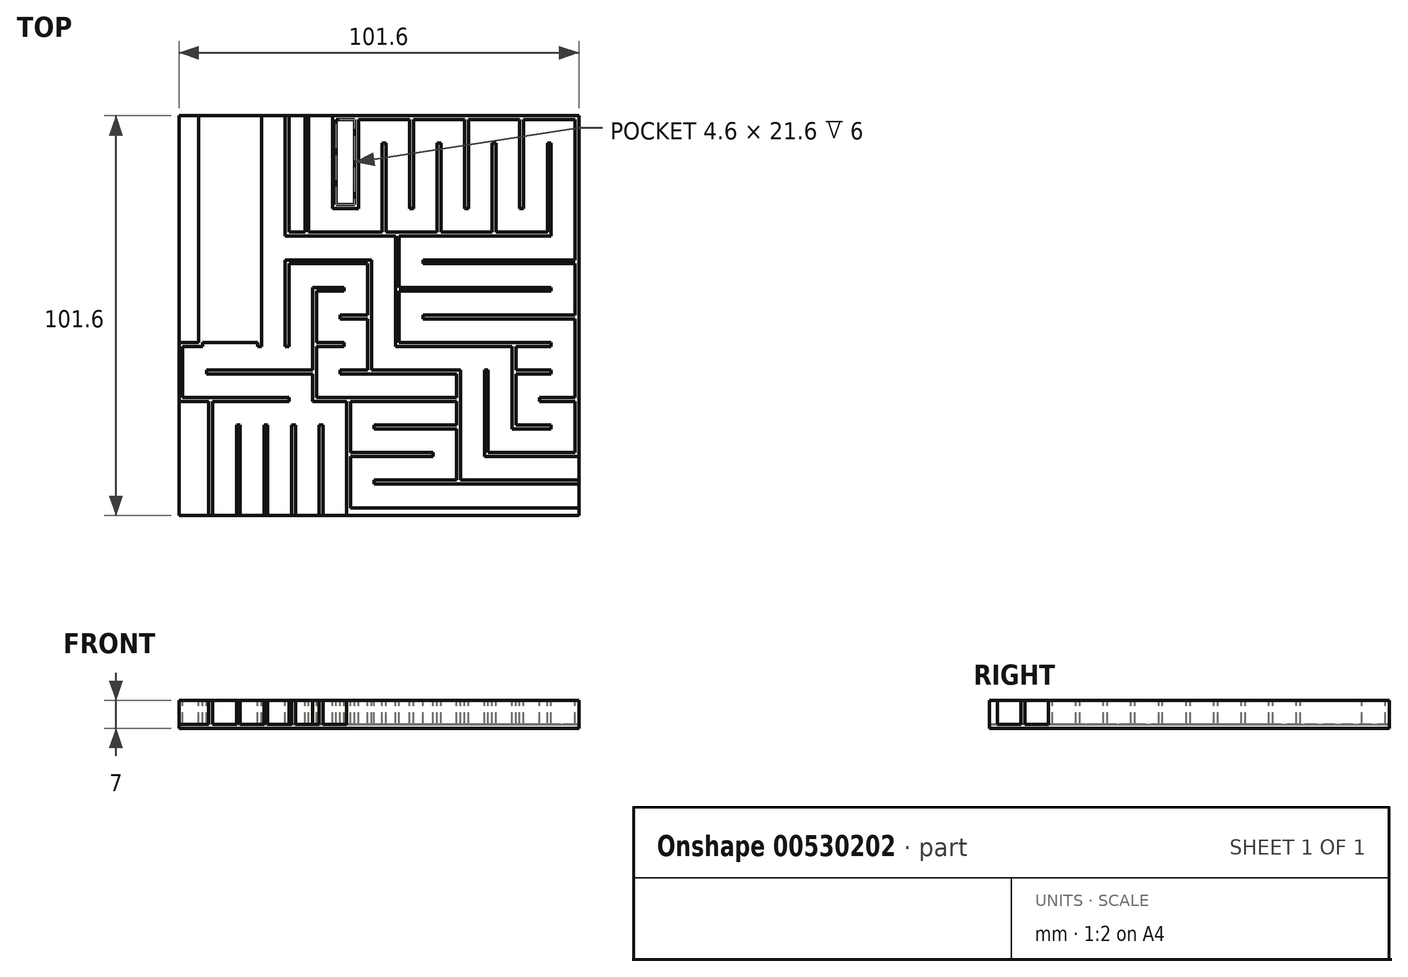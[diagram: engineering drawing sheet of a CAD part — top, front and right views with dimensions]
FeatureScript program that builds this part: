
annotation { "Feature Type Name" : "Feature", "Feature Type Description" : "" }
export const myFeature = defineFeature(function(context is Context, id is Id, definition is map)
    precondition{}
    {
        {
            var Q0;
            Q0=qCreatedBy(makeId("Top.planeOp"),FACE);
            var sketch = newSketch(context, id + "F0", { "sketchPlane" : qUnion([Q0])});
            skLineSegment(sketch, "E0.bottom", {"start": v(50.8, 50.8) * mm, "end": v(-50.8, 50.8) * mm});
            skLineSegment(sketch, "E0.top", {"start": v(50.8, -50.8) * mm, "end": v(-50.8, -50.8) * mm});
            skLineSegment(sketch, "E0.left", {"start": v(50.8, 50.8) * mm, "end": v(50.8, -50.8) * mm});
            skLineSegment(sketch, "E0.right", {"start": v(-50.8, 50.8) * mm, "end": v(-50.8, -50.8) * mm});
            skPoint(sketch, "E0.middle", {"position": v(0, 0) * mm});
            skSolve(sketch);
        }
        {
            var Q0;
            Q0=makeQuery(id+"F0.imprint","IMPRINT",FACE,{"disambiguationData":[TD([[makeQuery(id+"F0.imprint","IMPRINT",EDGE,{"derivedFrom":sQuery(id+"F0.wireOp",EDGE,"E0.bottom")}),1.0]])]});
            extrude(context, id + "F1", {"entities" : qUnion([Q0]), "depth" : 7 * mm, "offsetDistance" : 25.4 * mm});
        }
        {
            var Q0;
            Q0=makeQuery(id+"F1.opExtrude","CAP_FACE",FACE,{"disambiguationData":[OSD([sQuery(id+"F0.wireOp",EDGE,"E0.bottom"),sQuery(id+"F0.wireOp",EDGE,"E0.top"),sQuery(id+"F0.wireOp",EDGE,"E0.left"),sQuery(id+"F0.wireOp",EDGE,"E0.right")])],"isStart":false});
            var sketch = newSketch(context, id + "F2", { "sketchPlane" : qUnion([Q0])});
            skPoint(sketch, "E1", {"position": v(50.8, -48.8) * mm});
            skPoint(sketch, "E2", {"position": v(50.8, -42.8) * mm});
            skPoint(sketch, "E3", {"position": v(-1.2, -41.8) * mm});
            skLineSegment(sketch, "E4.bottom", {"start": v(-1.2, -41.8) * mm, "end": v(50.8, -41.8) * mm});
            skLineSegment(sketch, "E4.top", {"start": v(-1.2, -42.8) * mm, "end": v(50.8, -42.8) * mm});
            skLineSegment(sketch, "E4.left", {"start": v(-1.2, -41.8) * mm, "end": v(-1.2, -42.8) * mm});
            skLineSegment(sketch, "E4.right", {"start": v(50.8, -41.8) * mm, "end": v(50.8, -42.8) * mm});
            skPoint(sketch, "E5", {"position": v(13.8, -35.8) * mm});
            skPoint(sketch, "E6", {"position": v(-8.2, -34.8) * mm});
            skLineSegment(sketch, "E7.bottom", {"start": v(13.8, -35.8) * mm, "end": v(-8.2, -35.8) * mm});
            skLineSegment(sketch, "E7.top", {"start": v(13.8, -34.8) * mm, "end": v(-8.2, -34.8) * mm});
            skLineSegment(sketch, "E7.left", {"start": v(13.8, -35.8) * mm, "end": v(13.8, -34.8) * mm});
            skLineSegment(sketch, "E7.right", {"start": v(-8.2, -35.8) * mm, "end": v(-8.2, -34.8) * mm});
            skPoint(sketch, "E8", {"position": v(-7.2, -50.8) * mm});
            skLineSegment(sketch, "E9.bottom", {"start": v(-7.2, -50.8) * mm, "end": v(-8.2, -50.8) * mm});
            skLineSegment(sketch, "E9.top", {"start": v(-7.2, -34.8) * mm, "end": v(-8.2, -34.8) * mm});
            skLineSegment(sketch, "E9.left", {"start": v(-7.2, -50.8) * mm, "end": v(-7.2, -34.8) * mm});
            skLineSegment(sketch, "E9.right", {"start": v(-8.2, -50.8) * mm, "end": v(-8.2, -34.8) * mm});
            skLineSegment(sketch, "E10", {"start": v(50.8, -48.8) * mm, "end": v(-7.2, -48.8) * mm});
            skPoint(sketch, "E11", {"position": v(19.8, -28.8) * mm});
            skLineSegment(sketch, "E12", {"start": v(19.8, -28.8) * mm, "end": v(19.8, -41.8) * mm});
            skPoint(sketch, "E13", {"position": v(-1.2, -27.8) * mm});
            skLineSegment(sketch, "E14.bottom", {"start": v(-1.2, -27.8) * mm, "end": v(19.8, -27.8) * mm});
            skLineSegment(sketch, "E14.top", {"start": v(-1.2, -28.8) * mm, "end": v(19.8, -28.8) * mm});
            skLineSegment(sketch, "E14.left", {"start": v(-1.2, -27.8) * mm, "end": v(-1.2, -28.8) * mm});
            skLineSegment(sketch, "E14.right", {"start": v(19.8, -27.8) * mm, "end": v(19.8, -28.8) * mm});
            skPoint(sketch, "E15", {"position": v(19.8, -21.8) * mm});
            skLineSegment(sketch, "E16", {"start": v(19.8, -21.8) * mm, "end": v(19.8, -27.8) * mm});
            skPoint(sketch, "E17", {"position": v(-7.2, -21.8) * mm});
            skLineSegment(sketch, "E18", {"start": v(-7.2, -34.8) * mm, "end": v(-7.2, -21.8) * mm});
            skLineSegment(sketch, "E19", {"start": v(19.8, -21.8) * mm, "end": v(-7.2, -21.8) * mm});
            skSolve(sketch);
        }
        {
            var Q0;
            {var subQ6=sQuery(id+"F2.wireOp",EDGE,"E4.top");Q0=makeQuery(id+"F2.imprint","IMPRINT",FACE,{"disambiguationData":[TD([[makeQuery(id+"F2.imprint","IMPRINT",EDGE,{"derivedFrom":subQ6}),-1.0]])]});}
            extrude(context, id + "F3", {"entities" : qUnion([Q0]), "operationType" : NewBodyOperationType.REMOVE, "oppositeDirection" : true, "depth" : 6 * mm, "offsetDistance" : 25.4 * mm});
        }
        {
            var Q0;
            Q0=makeQuery(id+"F1.opExtrude","CAP_FACE",FACE,{"disambiguationData":[OSD([sQuery(id+"F0.wireOp",EDGE,"E0.bottom"),sQuery(id+"F0.wireOp",EDGE,"E0.top"),sQuery(id+"F0.wireOp",EDGE,"E0.left"),sQuery(id+"F0.wireOp",EDGE,"E0.right")])],"isStart":false});
            var sketch = newSketch(context, id + "F4", { "sketchPlane" : qUnion([Q0])});
            skPoint(sketch, "E20", {"position": v(-45.8, 50.8) * mm});
            skPoint(sketch, "E21", {"position": v(-38.8, 50.8) * mm});
            skPoint(sketch, "E22", {"position": v(-30.8, 50.8) * mm});
            skPoint(sketch, "E23", {"position": v(-44.8, -7.8) * mm});
            skLineSegment(sketch, "E24.bottom", {"start": v(-44.8, -7.8) * mm, "end": v(-45.8, -7.8) * mm});
            skLineSegment(sketch, "E24.top", {"start": v(-44.8, 50.8) * mm, "end": v(-45.8, 50.8) * mm});
            skLineSegment(sketch, "E24.left", {"start": v(-44.8, -7.8) * mm, "end": v(-44.8, 50.8) * mm});
            skLineSegment(sketch, "E24.right", {"start": v(-45.8, -7.8) * mm, "end": v(-45.8, 50.8) * mm});
            skPoint(sketch, "E25", {"position": v(-30.8, -6.8) * mm});
            skLineSegment(sketch, "E26.bottom", {"start": v(-30.8, -6.8) * mm, "end": v(-44.8, -6.8) * mm});
            skLineSegment(sketch, "E26.top", {"start": v(-30.8, -7.8) * mm, "end": v(-44.8, -7.8) * mm});
            skLineSegment(sketch, "E26.left", {"start": v(-30.8, -6.8) * mm, "end": v(-30.8, -7.8) * mm});
            skLineSegment(sketch, "E26.right", {"start": v(-44.8, -6.8) * mm, "end": v(-44.8, -7.8) * mm});
            skPoint(sketch, "E27", {"position": v(-50.8, -7.8) * mm});
            skLineSegment(sketch, "E28.bottom", {"start": v(-50.8, -7.8) * mm, "end": v(-45.8, -7.8) * mm});
            skLineSegment(sketch, "E28.top", {"start": v(-50.8, -7.8) * mm, "end": v(-45.8, -7.8) * mm});
            skLineSegment(sketch, "E28.left", {"start": v(-50.8, -7.8) * mm, "end": v(-50.8, -7.8) * mm});
            skLineSegment(sketch, "E28.right", {"start": v(-45.8, -7.8) * mm, "end": v(-45.8, -7.8) * mm});
            skLineSegment(sketch, "E29", {"start": v(-30.8, -6.8) * mm, "end": v(-30.8, 50.8) * mm});
            skPoint(sketch, "E30", {"position": v(-37.8, -0.8) * mm});
            skLineSegment(sketch, "E31.bottom", {"start": v(-37.8, -0.8) * mm, "end": v(-38.8, -0.8) * mm});
            skLineSegment(sketch, "E31.top", {"start": v(-37.8, 50.8) * mm, "end": v(-38.8, 50.8) * mm});
            skLineSegment(sketch, "E31.left", {"start": v(-37.8, -0.8) * mm, "end": v(-37.8, 50.8) * mm});
            skLineSegment(sketch, "E31.right", {"start": v(-38.8, -0.8) * mm, "end": v(-38.8, 50.8) * mm});
            skLineSegment(sketch, "E32.bottom", {"start": v(-50.8, -7.8) * mm, "end": v(-30.8, -7.8) * mm});
            skLineSegment(sketch, "E32.top", {"start": v(-50.8, -6.8) * mm, "end": v(-30.8, -6.8) * mm});
            skLineSegment(sketch, "E32.left", {"start": v(-50.8, -7.8) * mm, "end": v(-50.8, -6.8) * mm});
            skLineSegment(sketch, "E32.right", {"start": v(-30.8, -7.8) * mm, "end": v(-30.8, -6.8) * mm});
            skSolve(sketch);
        }
        {
            var Q0;
            {var subQ0=sQuery(id+"F4.wireOp",EDGE,"E24.right");var subQ3=sQuery(id+"F4.wireOp",EDGE,"E32.top");var subQ4=makeQuery(id+"F4.imprint","INTERSECT",VERTEX,{"derivedFrom":[subQ0,subQ3]});Q0=makeQuery(id+"F4.imprint","IMPRINT",FACE,{"disambiguationData":[TD([[makeQuery(id+"F4.imprint","IMPRINT",EDGE,{"disambiguationData":[TD([[subQ4,-1.0]])],"derivedFrom":subQ0}),1.0]])]});}
            var Q1;
            {var subQ2=sQuery(id+"F4.wireOp",EDGE,"E24.left");Q1=makeQuery(id+"F4.imprint","IMPRINT",FACE,{"disambiguationData":[TD([[makeQuery(id+"F4.imprint","IMPRINT",EDGE,{"derivedFrom":subQ2}),-1.0]])]});}
            extrude(context, id + "F5", {"entities" : qUnion([Q0, Q1]), "operationType" : NewBodyOperationType.REMOVE, "oppositeDirection" : true, "depth" : 6 * mm, "offsetDistance" : 25.4 * mm});
        }
        {
            var Q0;
            {var subQ1=sQuery(id+"F0.wireOp",EDGE,"E0.left");var subQ2=sQuery(id+"F0.wireOp",EDGE,"E0.top");var subQ3=sQuery(id+"F0.wireOp",EDGE,"E0.right");var subQ5=sQuery(id+"F0.wireOp",EDGE,"E0.bottom");Q0=makeQuery(id+"F5.boolean.opBoolean","SPLIT",FACE,{"disambiguationData":[TD([makeQuery(id+"F1.opExtrude","SWEPT_FACE",FACE,{"disambiguationData":[OSD([subQ2])]})])],"derivedFrom":makeQuery(id+"F1.opExtrude","CAP_FACE",FACE,{"disambiguationData":[OSD([subQ5,subQ2,subQ1,subQ3])],"isStart":false})});}
            var sketch = newSketch(context, id + "F6", { "sketchPlane" : qUnion([Q0])});
            skPoint(sketch, "E33", {"position": v(-18.8, 50.8) * mm});
            skPoint(sketch, "E34", {"position": v(-11.8, 50.8) * mm});
            skPoint(sketch, "E35", {"position": v(-23.8, 50.8) * mm});
            skPoint(sketch, "E36", {"position": v(-29.8, 21.2) * mm});
            skLineSegment(sketch, "E37.bottom", {"start": v(-29.8, 21.2) * mm, "end": v(-30.8, 21.2) * mm});
            skLineSegment(sketch, "E37.top", {"start": v(-29.8, 50.8) * mm, "end": v(-30.8, 50.8) * mm});
            skLineSegment(sketch, "E37.left", {"start": v(-29.8, 21.2) * mm, "end": v(-29.8, 50.8) * mm});
            skLineSegment(sketch, "E37.right", {"start": v(-30.8, 21.2) * mm, "end": v(-30.8, 50.8) * mm});
            skPoint(sketch, "E38", {"position": v(-22.8, 21.2) * mm});
            skLineSegment(sketch, "E39.bottom", {"start": v(-22.8, 21.2) * mm, "end": v(-23.8, 21.2) * mm});
            skLineSegment(sketch, "E39.top", {"start": v(-22.8, 50.8) * mm, "end": v(-23.8, 50.8) * mm});
            skLineSegment(sketch, "E39.left", {"start": v(-22.8, 21.2) * mm, "end": v(-22.8, 50.8) * mm});
            skLineSegment(sketch, "E39.right", {"start": v(-23.8, 21.2) * mm, "end": v(-23.8, 50.8) * mm});
            skLineSegment(sketch, "E40", {"start": v(-29.8, 21.2) * mm, "end": v(-23.8, 21.2) * mm});
            skPoint(sketch, "E41", {"position": v(-17.8, 21.2) * mm});
            skLineSegment(sketch, "E42.bottom", {"start": v(-17.8, 21.2) * mm, "end": v(-18.8, 21.2) * mm});
            skLineSegment(sketch, "E42.top", {"start": v(-17.8, 50.8) * mm, "end": v(-18.8, 50.8) * mm});
            skLineSegment(sketch, "E42.left", {"start": v(-17.8, 21.2) * mm, "end": v(-17.8, 50.8) * mm});
            skLineSegment(sketch, "E42.right", {"start": v(-18.8, 21.2) * mm, "end": v(-18.8, 50.8) * mm});
            skLineSegment(sketch, "E43", {"start": v(-22.8, 21.2) * mm, "end": v(-18.8, 21.2) * mm});
            skPoint(sketch, "E44", {"position": v(49.8, 49.8) * mm});
            skLineSegment(sketch, "E45.bottom", {"start": v(-11.8, 50.8) * mm, "end": v(49.8, 50.8) * mm});
            skLineSegment(sketch, "E45.top", {"start": v(-11.8, 49.8) * mm, "end": v(49.8, 49.8) * mm});
            skLineSegment(sketch, "E45.left", {"start": v(-11.8, 50.8) * mm, "end": v(-11.8, 49.8) * mm});
            skLineSegment(sketch, "E45.right", {"start": v(49.8, 50.8) * mm, "end": v(49.8, 49.8) * mm});
            skPoint(sketch, "E46", {"position": v(-10.8, 27.2) * mm});
            skLineSegment(sketch, "E47.bottom", {"start": v(-10.8, 27.2) * mm, "end": v(-11.8, 27.2) * mm});
            skLineSegment(sketch, "E47.top", {"start": v(-10.8, 50.8) * mm, "end": v(-11.8, 50.8) * mm});
            skLineSegment(sketch, "E47.left", {"start": v(-10.8, 27.2) * mm, "end": v(-10.8, 50.8) * mm});
            skLineSegment(sketch, "E47.right", {"start": v(-11.8, 27.2) * mm, "end": v(-11.8, 50.8) * mm});
            skPoint(sketch, "E48", {"position": v(0.8, 43.8) * mm});
            skPoint(sketch, "E49", {"position": v(1.8, 21.2) * mm});
            skLineSegment(sketch, "E50", {"start": v(-17.8, 21.2) * mm, "end": v(1.8, 21.2) * mm});
            skLineSegment(sketch, "E51.bottom", {"start": v(1.8, 21.2) * mm, "end": v(0.8, 21.2) * mm});
            skLineSegment(sketch, "E51.top", {"start": v(1.8, 43.8) * mm, "end": v(0.8, 43.8) * mm});
            skLineSegment(sketch, "E51.left", {"start": v(1.8, 21.2) * mm, "end": v(1.8, 43.8) * mm});
            skLineSegment(sketch, "E51.right", {"start": v(0.8, 21.2) * mm, "end": v(0.8, 43.8) * mm});
            skPoint(sketch, "E52", {"position": v(50.8, 21.2) * mm});
            skLineSegment(sketch, "E53.bottom", {"start": v(50.8, 21.2) * mm, "end": v(49.8, 21.2) * mm});
            skLineSegment(sketch, "E53.top", {"start": v(50.8, 50.8) * mm, "end": v(49.8, 50.8) * mm});
            skLineSegment(sketch, "E53.left", {"start": v(50.8, 21.2) * mm, "end": v(50.8, 50.8) * mm});
            skLineSegment(sketch, "E53.right", {"start": v(49.8, 21.2) * mm, "end": v(49.8, 50.8) * mm});
            skLineSegment(sketch, "E54", {"start": v(1.8, 21.2) * mm, "end": v(43.8, 21.2) * mm});
            skPoint(sketch, "E55", {"position": v(42.8, 43.8) * mm});
            skLineSegment(sketch, "E56.bottom", {"start": v(43.8, 21.2) * mm, "end": v(42.8, 21.2) * mm});
            skLineSegment(sketch, "E56.top", {"start": v(43.8, 43.8) * mm, "end": v(42.8, 43.8) * mm});
            skLineSegment(sketch, "E56.left", {"start": v(43.8, 21.2) * mm, "end": v(43.8, 43.8) * mm});
            skLineSegment(sketch, "E56.right", {"start": v(42.8, 21.2) * mm, "end": v(42.8, 43.8) * mm});
            skPoint(sketch, "E57", {"position": v(36.8, 27.2) * mm});
            skPoint(sketch, "E58", {"position": v(35.8, 49.8) * mm});
            skLineSegment(sketch, "E59.bottom", {"start": v(36.8, 27.2) * mm, "end": v(35.8, 27.2) * mm});
            skLineSegment(sketch, "E59.top", {"start": v(36.8, 49.8) * mm, "end": v(35.8, 49.8) * mm});
            skLineSegment(sketch, "E59.left", {"start": v(36.8, 27.2) * mm, "end": v(36.8, 49.8) * mm});
            skLineSegment(sketch, "E59.right", {"start": v(35.8, 27.2) * mm, "end": v(35.8, 49.8) * mm});
            skPoint(sketch, "E60", {"position": v(29.8, 43.8) * mm});
            skPoint(sketch, "E61", {"position": v(28.8, 21.2) * mm});
            skLineSegment(sketch, "E62.bottom", {"start": v(28.8, 21.2) * mm, "end": v(29.8, 21.2) * mm});
            skLineSegment(sketch, "E62.top", {"start": v(28.8, 43.8) * mm, "end": v(29.8, 43.8) * mm});
            skLineSegment(sketch, "E62.left", {"start": v(28.8, 21.2) * mm, "end": v(28.8, 43.8) * mm});
            skLineSegment(sketch, "E62.right", {"start": v(29.8, 21.2) * mm, "end": v(29.8, 43.8) * mm});
            skLineSegment(sketch, "E63.bottom", {"start": v(43.8, 21.2) * mm, "end": v(49.8, 21.2) * mm});
            skLineSegment(sketch, "E63.top", {"start": v(43.8, 21.2) * mm, "end": v(49.8, 21.2) * mm});
            skLineSegment(sketch, "E63.left", {"start": v(43.8, 21.2) * mm, "end": v(43.8, 21.2) * mm});
            skLineSegment(sketch, "E63.right", {"start": v(49.8, 21.2) * mm, "end": v(49.8, 21.2) * mm});
            skPoint(sketch, "E64", {"position": v(22.8, 27.2) * mm});
            skPoint(sketch, "E65", {"position": v(21.8, 49.8) * mm});
            skLineSegment(sketch, "E66.bottom", {"start": v(21.8, 49.8) * mm, "end": v(22.8, 49.8) * mm});
            skLineSegment(sketch, "E66.top", {"start": v(21.8, 27.2) * mm, "end": v(22.8, 27.2) * mm});
            skLineSegment(sketch, "E66.left", {"start": v(21.8, 49.8) * mm, "end": v(21.8, 27.2) * mm});
            skLineSegment(sketch, "E66.right", {"start": v(22.8, 49.8) * mm, "end": v(22.8, 27.2) * mm});
            skPoint(sketch, "E67", {"position": v(15.8, 43.8) * mm});
            skPoint(sketch, "E68", {"position": v(14.8, 21.2) * mm});
            skLineSegment(sketch, "E69.bottom", {"start": v(14.8, 21.2) * mm, "end": v(15.8, 21.2) * mm});
            skLineSegment(sketch, "E69.top", {"start": v(14.8, 43.8) * mm, "end": v(15.8, 43.8) * mm});
            skLineSegment(sketch, "E69.left", {"start": v(14.8, 21.2) * mm, "end": v(14.8, 43.8) * mm});
            skLineSegment(sketch, "E69.right", {"start": v(15.8, 21.2) * mm, "end": v(15.8, 43.8) * mm});
            skPoint(sketch, "E70", {"position": v(8.8, 27.2) * mm});
            skPoint(sketch, "E71", {"position": v(7.8, 49.8) * mm});
            skLineSegment(sketch, "E72.bottom", {"start": v(7.8, 49.8) * mm, "end": v(8.8, 49.8) * mm});
            skLineSegment(sketch, "E72.top", {"start": v(7.8, 27.2) * mm, "end": v(8.8, 27.2) * mm});
            skLineSegment(sketch, "E72.left", {"start": v(7.8, 49.8) * mm, "end": v(7.8, 27.2) * mm});
            skLineSegment(sketch, "E72.right", {"start": v(8.8, 49.8) * mm, "end": v(8.8, 27.2) * mm});
            skPoint(sketch, "E73", {"position": v(-5.2, 27.2) * mm});
            skPoint(sketch, "E74", {"position": v(-6.2, 49.8) * mm});
            skLineSegment(sketch, "E75.bottom", {"start": v(-5.2, 27.2) * mm, "end": v(-6.2, 27.2) * mm});
            skLineSegment(sketch, "E75.top", {"start": v(-5.2, 49.8) * mm, "end": v(-6.2, 49.8) * mm});
            skLineSegment(sketch, "E75.left", {"start": v(-5.2, 27.2) * mm, "end": v(-5.2, 49.8) * mm});
            skLineSegment(sketch, "E75.right", {"start": v(-6.2, 27.2) * mm, "end": v(-6.2, 49.8) * mm});
            skPoint(sketch, "E76", {"position": v(-11.8, 28.2) * mm});
            skLineSegment(sketch, "E77.bottom", {"start": v(-11.8, 28.2) * mm, "end": v(-5.2, 28.2) * mm});
            skLineSegment(sketch, "E77.top", {"start": v(-11.8, 27.2) * mm, "end": v(-5.2, 27.2) * mm});
            skLineSegment(sketch, "E77.left", {"start": v(-11.8, 28.2) * mm, "end": v(-11.8, 27.2) * mm});
            skLineSegment(sketch, "E77.right", {"start": v(-5.2, 28.2) * mm, "end": v(-5.2, 27.2) * mm});
            skSolve(sketch);
        }
        {
            var Q0;
            {var subQ0=sQuery(id+"F6.wireOp",EDGE,"E37.left");Q0=makeQuery(id+"F6.imprint","IMPRINT",FACE,{"disambiguationData":[TD([[makeQuery(id+"F6.imprint","IMPRINT",EDGE,{"derivedFrom":subQ0}),-1.0]])]});}
            var Q1;
            {var subQ0=sQuery(id+"F6.wireOp",EDGE,"E39.left");Q1=makeQuery(id+"F6.imprint","IMPRINT",FACE,{"disambiguationData":[TD([[makeQuery(id+"F6.imprint","IMPRINT",EDGE,{"derivedFrom":subQ0}),-1.0]])]});}
            var Q2;
            {var subQ24=sQuery(id+"F6.wireOp",EDGE,"E42.left");Q2=makeQuery(id+"F6.imprint","IMPRINT",FACE,{"disambiguationData":[TD([[makeQuery(id+"F6.imprint","IMPRINT",EDGE,{"derivedFrom":subQ24}),-1.0]])]});}
            var Q3;
            {var subQ1=sQuery(id+"F6.wireOp",EDGE,"E45.top");var subQ3=sQuery(id+"F6.wireOp",EDGE,"E47.left");var subQ4=makeQuery(id+"F6.imprint","INTERSECT",VERTEX,{"derivedFrom":[subQ1,subQ3]});Q3=makeQuery(id+"F6.imprint","IMPRINT",FACE,{"disambiguationData":[TD([[makeQuery(id+"F6.imprint","IMPRINT",EDGE,{"disambiguationData":[TD([[subQ4,1.0]])],"derivedFrom":subQ3}),-1.0]])]});}
            extrude(context, id + "F7", {"entities" : qUnion([Q0, Q1, Q2, Q3]), "operationType" : NewBodyOperationType.REMOVE, "oppositeDirection" : true, "depth" : 6 * mm, "offsetDistance" : 25.4 * mm});
        }
        {
            var Q0;
            {var subQ1=sQuery(id+"F0.wireOp",EDGE,"E0.left");var subQ2=sQuery(id+"F0.wireOp",EDGE,"E0.top");var subQ3=sQuery(id+"F0.wireOp",EDGE,"E0.right");var subQ5=sQuery(id+"F0.wireOp",EDGE,"E0.bottom");Q0=makeQuery(id+"F5.boolean.opBoolean","SPLIT",FACE,{"disambiguationData":[TD([makeQuery(id+"F1.opExtrude","SWEPT_FACE",FACE,{"disambiguationData":[OSD([subQ2])]})])],"derivedFrom":makeQuery(id+"F1.opExtrude","CAP_FACE",FACE,{"disambiguationData":[OSD([subQ5,subQ2,subQ1,subQ3])],"isStart":false})});}
            var sketch = newSketch(context, id + "F8", { "sketchPlane" : qUnion([Q0])});
            skPoint(sketch, "E78", {"position": v(-30.8, 14.2) * mm});
            skLineSegment(sketch, "E79.bottom", {"start": v(-30.8, 14.2) * mm, "end": v(-29.8, 14.2) * mm});
            skLineSegment(sketch, "E79.top", {"start": v(-30.8, 21.2) * mm, "end": v(-29.8, 21.2) * mm});
            skLineSegment(sketch, "E79.left", {"start": v(-30.8, 14.2) * mm, "end": v(-30.8, 21.2) * mm});
            skLineSegment(sketch, "E79.right", {"start": v(-29.8, 14.2) * mm, "end": v(-29.8, 21.2) * mm});
            skPoint(sketch, "E80", {"position": v(-1.8, 14.2) * mm});
            skPoint(sketch, "E81", {"position": v(4.2, 20.2) * mm});
            skLineSegment(sketch, "E82.bottom", {"start": v(4.2, 20.2) * mm, "end": v(-22.8, 20.2) * mm});
            skLineSegment(sketch, "E82.top", {"start": v(4.2, 21.2) * mm, "end": v(-22.8, 21.2) * mm});
            skLineSegment(sketch, "E82.left", {"start": v(4.2, 20.2) * mm, "end": v(4.2, 21.2) * mm});
            skLineSegment(sketch, "E82.right", {"start": v(-22.8, 20.2) * mm, "end": v(-22.8, 21.2) * mm});
            skLineSegment(sketch, "E83", {"start": v(-22.8, 21.2) * mm, "end": v(-29.8, 21.2) * mm});
            skPoint(sketch, "E84", {"position": v(-23.8, 21.2) * mm});
            skLineSegment(sketch, "E85.bottom", {"start": v(-23.8, 21.2) * mm, "end": v(-22.8, 21.2) * mm});
            skLineSegment(sketch, "E85.top", {"start": v(-23.8, 20.2) * mm, "end": v(-22.8, 20.2) * mm});
            skLineSegment(sketch, "E85.left", {"start": v(-23.8, 21.2) * mm, "end": v(-23.8, 20.2) * mm});
            skLineSegment(sketch, "E85.right", {"start": v(-22.8, 21.2) * mm, "end": v(-22.8, 20.2) * mm});
            skLineSegment(sketch, "E86", {"start": v(-29.8, 14.2) * mm, "end": v(-1.8, 14.2) * mm});
            skLineSegment(sketch, "E87.bottom", {"start": v(19.8, -41.8) * mm, "end": v(50.8, -41.8) * mm});
            skLineSegment(sketch, "E87.top", {"start": v(19.8, -42.8) * mm, "end": v(50.8, -42.8) * mm});
            skLineSegment(sketch, "E87.left", {"start": v(19.8, -41.8) * mm, "end": v(19.8, -42.8) * mm});
            skLineSegment(sketch, "E87.right", {"start": v(50.8, -41.8) * mm, "end": v(50.8, -42.8) * mm});
            skPoint(sketch, "E88", {"position": v(20.8, -13.8) * mm});
            skLineSegment(sketch, "E89.bottom", {"start": v(20.8, -13.8) * mm, "end": v(19.8, -13.8) * mm});
            skLineSegment(sketch, "E89.top", {"start": v(20.8, -41.8) * mm, "end": v(19.8, -41.8) * mm});
            skLineSegment(sketch, "E89.left", {"start": v(20.8, -13.8) * mm, "end": v(20.8, -41.8) * mm});
            skLineSegment(sketch, "E89.right", {"start": v(19.8, -13.8) * mm, "end": v(19.8, -41.8) * mm});
            skPoint(sketch, "E90", {"position": v(-1.8, -13.8) * mm});
            skLineSegment(sketch, "E91", {"start": v(-1.8, -13.8) * mm, "end": v(-1.8, 14.2) * mm});
            skLineSegment(sketch, "E92", {"start": v(-1.8, -13.8) * mm, "end": v(19.8, -13.8) * mm});
            skPoint(sketch, "E93", {"position": v(50.8, -35.8) * mm});
            skPoint(sketch, "E94", {"position": v(26.8, -34.8) * mm});
            skLineSegment(sketch, "E95.bottom", {"start": v(26.8, -34.8) * mm, "end": v(50.8, -34.8) * mm});
            skLineSegment(sketch, "E95.top", {"start": v(26.8, -35.8) * mm, "end": v(50.8, -35.8) * mm});
            skLineSegment(sketch, "E95.left", {"start": v(26.8, -34.8) * mm, "end": v(26.8, -35.8) * mm});
            skLineSegment(sketch, "E95.right", {"start": v(50.8, -34.8) * mm, "end": v(50.8, -35.8) * mm});
            skPoint(sketch, "E96", {"position": v(27.8, -6.8) * mm});
            skLineSegment(sketch, "E97.bottom", {"start": v(27.8, -6.8) * mm, "end": v(26.8, -6.8) * mm});
            skLineSegment(sketch, "E97.top", {"start": v(27.8, -34.8) * mm, "end": v(26.8, -34.8) * mm});
            skLineSegment(sketch, "E97.left", {"start": v(27.8, -6.8) * mm, "end": v(27.8, -34.8) * mm});
            skLineSegment(sketch, "E97.right", {"start": v(26.8, -6.8) * mm, "end": v(26.8, -34.8) * mm});
            skPoint(sketch, "E98", {"position": v(4.2, -6.8) * mm});
            skLineSegment(sketch, "E99", {"start": v(4.2, 20.2) * mm, "end": v(4.2, -6.8) * mm});
            skLineSegment(sketch, "E100", {"start": v(26.8, -6.8) * mm, "end": v(4.2, -6.8) * mm});
            skSolve(sketch);
        }
        {
            var Q0;
            Q0=makeQuery(id+"F8.imprint","IMPRINT",FACE,{"disambiguationData":[TD([[makeQuery(id+"F8.imprint","IMPRINT",EDGE,{"derivedFrom":sQuery(id+"F8.wireOp",EDGE,"E79.right")}),-1.0]])]});
            extrude(context, id + "F9", {"entities" : qUnion([Q0]), "operationType" : NewBodyOperationType.REMOVE, "oppositeDirection" : true, "depth" : 6 * mm, "offsetDistance" : 25.4 * mm});
        }
        {
            var Q0;
            {var subQ16=sQuery(id+"F0.wireOp",EDGE,"E0.left");var subQ18=sQuery(id+"F0.wireOp",EDGE,"E0.bottom");var subQ29=sQuery(id+"F0.wireOp",EDGE,"E0.top");var subQ30=sQuery(id+"F0.wireOp",EDGE,"E0.right");Q0=makeQuery(id+"F9.boolean.opBoolean","SPLIT",FACE,{"disambiguationData":[TD([makeQuery(id+"F7.boolean.opBoolean","COPY",FACE,{"derivedFrom":makeQuery(id+"F7.opExtrude","SWEPT_FACE",FACE,{"disambiguationData":[OSD([sQuery(id+"F6.wireOp",EDGE,"E39.left")])]})})])],"derivedFrom":makeQuery(id+"F5.boolean.opBoolean","SPLIT",FACE,{"disambiguationData":[TD([makeQuery(id+"F1.opExtrude","SWEPT_FACE",FACE,{"disambiguationData":[OSD([subQ29])]})])],"derivedFrom":makeQuery(id+"F1.opExtrude","CAP_FACE",FACE,{"disambiguationData":[OSD([subQ18,subQ29,subQ16,subQ30])],"isStart":false})})});}
            var sketch = newSketch(context, id + "F10", { "sketchPlane" : qUnion([Q0])});
            skLineSegment(sketch, "E101.bottom", {"start": v(43.8, 21.2) * mm, "end": v(4.2, 21.2) * mm});
            skLineSegment(sketch, "E101.top", {"start": v(43.8, 20.2) * mm, "end": v(4.2, 20.2) * mm});
            skLineSegment(sketch, "E101.left", {"start": v(43.8, 21.2) * mm, "end": v(43.8, 20.2) * mm});
            skLineSegment(sketch, "E101.right", {"start": v(4.2, 21.2) * mm, "end": v(4.2, 20.2) * mm});
            skLineSegment(sketch, "E102.bottom", {"start": v(50.8, -35.8) * mm, "end": v(49.8, -35.8) * mm});
            skLineSegment(sketch, "E102.top", {"start": v(50.8, 21.2) * mm, "end": v(49.8, 21.2) * mm});
            skLineSegment(sketch, "E102.left", {"start": v(50.8, -35.8) * mm, "end": v(50.8, 21.2) * mm});
            skLineSegment(sketch, "E102.right", {"start": v(49.8, -35.8) * mm, "end": v(49.8, 21.2) * mm});
            skPoint(sketch, "E103", {"position": v(5.2, -6.8) * mm});
            skLineSegment(sketch, "E104.bottom", {"start": v(5.2, -6.8) * mm, "end": v(4.2, -6.8) * mm});
            skLineSegment(sketch, "E104.top", {"start": v(5.2, 21.2) * mm, "end": v(4.2, 21.2) * mm});
            skLineSegment(sketch, "E104.left", {"start": v(5.2, -6.8) * mm, "end": v(5.2, 21.2) * mm});
            skLineSegment(sketch, "E104.right", {"start": v(4.2, -6.8) * mm, "end": v(4.2, 21.2) * mm});
            skPoint(sketch, "E105", {"position": v(26.8, -5.8) * mm});
            skLineSegment(sketch, "E106.top", {"start": v(26.8, -6.8) * mm, "end": v(5.2, -6.8) * mm});
            skLineSegment(sketch, "E106.left", {"start": v(26.8, -5.8) * mm, "end": v(26.8, -6.8) * mm});
            skLineSegment(sketch, "E106.right", {"start": v(5.2, -5.8) * mm, "end": v(5.2, -6.8) * mm});
            skPoint(sketch, "E107", {"position": v(11.2, 14.2) * mm});
            skPoint(sketch, "E108", {"position": v(49.8, 13.2) * mm});
            skLineSegment(sketch, "E109.bottom", {"start": v(11.2, 14.2) * mm, "end": v(49.8, 14.2) * mm});
            skLineSegment(sketch, "E109.top", {"start": v(11.2, 13.2) * mm, "end": v(49.8, 13.2) * mm});
            skLineSegment(sketch, "E109.left", {"start": v(11.2, 14.2) * mm, "end": v(11.2, 13.2) * mm});
            skLineSegment(sketch, "E109.right", {"start": v(49.8, 14.2) * mm, "end": v(49.8, 13.2) * mm});
            skPoint(sketch, "E110", {"position": v(43.8, 7.2) * mm});
            skPoint(sketch, "E111", {"position": v(5.2, 6.2) * mm});
            skLineSegment(sketch, "E112.bottom", {"start": v(5.2, 6.2) * mm, "end": v(43.8, 6.2) * mm});
            skLineSegment(sketch, "E112.top", {"start": v(5.2, 7.2) * mm, "end": v(43.8, 7.2) * mm});
            skLineSegment(sketch, "E112.left", {"start": v(5.2, 6.2) * mm, "end": v(5.2, 7.2) * mm});
            skLineSegment(sketch, "E112.right", {"start": v(43.8, 6.2) * mm, "end": v(43.8, 7.2) * mm});
            skPoint(sketch, "E113", {"position": v(11.2, 0.2) * mm});
            skPoint(sketch, "E114", {"position": v(49.8, -0.8) * mm});
            skLineSegment(sketch, "E115.bottom", {"start": v(11.2, 0.2) * mm, "end": v(49.8, 0.2) * mm});
            skLineSegment(sketch, "E115.top", {"start": v(11.2, -0.8) * mm, "end": v(49.8, -0.8) * mm});
            skLineSegment(sketch, "E115.left", {"start": v(11.2, 0.2) * mm, "end": v(11.2, -0.8) * mm});
            skLineSegment(sketch, "E115.right", {"start": v(49.8, 0.2) * mm, "end": v(49.8, -0.8) * mm});
            skPoint(sketch, "E116", {"position": v(26.8, -7.8) * mm});
            skLineSegment(sketch, "E117.left", {"start": v(26.8, -7.8) * mm, "end": v(26.8, -6.8) * mm});
            skLineSegment(sketch, "E117.right", {"start": v(49.8, -7.8) * mm, "end": v(49.8, -6.8) * mm});
            skPoint(sketch, "E118", {"position": v(43.8, -6.8) * mm});
            skLineSegment(sketch, "E119.bottom", {"start": v(26.8, -7.8) * mm, "end": v(43.8, -7.8) * mm});
            skLineSegment(sketch, "E119.top", {"start": v(26.8, -6.8) * mm, "end": v(43.8, -6.8) * mm});
            skLineSegment(sketch, "E119.right", {"start": v(43.8, -7.8) * mm, "end": v(43.8, -6.8) * mm});
            skLineSegment(sketch, "E120.bottom", {"start": v(26.8, -7.8) * mm, "end": v(4.2, -7.8) * mm});
            skLineSegment(sketch, "E120.top", {"start": v(26.8, -6.8) * mm, "end": v(4.2, -6.8) * mm});
            skLineSegment(sketch, "E120.right", {"start": v(4.2, -7.8) * mm, "end": v(4.2, -6.8) * mm});
            skPoint(sketch, "E121", {"position": v(27.8, -13.8) * mm});
            skLineSegment(sketch, "E122.bottom", {"start": v(26.8, -35.8) * mm, "end": v(27.8, -35.8) * mm});
            skLineSegment(sketch, "E122.top", {"start": v(26.8, -13.8) * mm, "end": v(27.8, -13.8) * mm});
            skLineSegment(sketch, "E122.left", {"start": v(26.8, -35.8) * mm, "end": v(26.8, -13.8) * mm});
            skLineSegment(sketch, "E122.right", {"start": v(27.8, -35.8) * mm, "end": v(27.8, -13.8) * mm});
            skPoint(sketch, "E123", {"position": v(49.8, -34.8) * mm});
            skPoint(sketch, "E124", {"position": v(49.8, -35.8) * mm});
            skLineSegment(sketch, "E125.bottom", {"start": v(49.8, -34.8) * mm, "end": v(27.8, -34.8) * mm});
            skLineSegment(sketch, "E125.top", {"start": v(49.8, -35.8) * mm, "end": v(27.8, -35.8) * mm});
            skLineSegment(sketch, "E125.left", {"start": v(49.8, -34.8) * mm, "end": v(49.8, -35.8) * mm});
            skLineSegment(sketch, "E125.right", {"start": v(27.8, -34.8) * mm, "end": v(27.8, -35.8) * mm});
            skPoint(sketch, "E126", {"position": v(33.8, -7.8) * mm});
            skPoint(sketch, "E127", {"position": v(34.8, -28.8) * mm});
            skLineSegment(sketch, "E128.bottom", {"start": v(34.8, -28.8) * mm, "end": v(33.8, -28.8) * mm});
            skLineSegment(sketch, "E128.top", {"start": v(34.8, -7.8) * mm, "end": v(33.8, -7.8) * mm});
            skLineSegment(sketch, "E128.left", {"start": v(34.8, -28.8) * mm, "end": v(34.8, -7.8) * mm});
            skLineSegment(sketch, "E128.right", {"start": v(33.8, -28.8) * mm, "end": v(33.8, -7.8) * mm});
            skPoint(sketch, "E129", {"position": v(43.8, -27.8) * mm});
            skLineSegment(sketch, "E130.bottom", {"start": v(43.8, -27.8) * mm, "end": v(34.8, -27.8) * mm});
            skLineSegment(sketch, "E130.top", {"start": v(43.8, -28.8) * mm, "end": v(34.8, -28.8) * mm});
            skLineSegment(sketch, "E130.left", {"start": v(43.8, -27.8) * mm, "end": v(43.8, -28.8) * mm});
            skLineSegment(sketch, "E130.right", {"start": v(34.8, -27.8) * mm, "end": v(34.8, -28.8) * mm});
            skPoint(sketch, "E131", {"position": v(40.8, -21.8) * mm});
            skPoint(sketch, "E132", {"position": v(49.8, -20.8) * mm});
            skLineSegment(sketch, "E133.bottom", {"start": v(40.8, -21.8) * mm, "end": v(49.8, -21.8) * mm});
            skLineSegment(sketch, "E133.top", {"start": v(40.8, -20.8) * mm, "end": v(49.8, -20.8) * mm});
            skLineSegment(sketch, "E133.left", {"start": v(40.8, -21.8) * mm, "end": v(40.8, -20.8) * mm});
            skLineSegment(sketch, "E133.right", {"start": v(49.8, -21.8) * mm, "end": v(49.8, -20.8) * mm});
            skPoint(sketch, "E134", {"position": v(43.8, -13.8) * mm});
            skPoint(sketch, "E135", {"position": v(34.8, -71.74) * mm});
            skPoint(sketch, "E136", {"position": v(34.8, -14.8) * mm});
            skLineSegment(sketch, "E137.bottom", {"start": v(34.8, -14.8) * mm, "end": v(43.8, -14.8) * mm});
            skLineSegment(sketch, "E137.top", {"start": v(34.8, -13.8) * mm, "end": v(43.8, -13.8) * mm});
            skLineSegment(sketch, "E137.left", {"start": v(34.8, -14.8) * mm, "end": v(34.8, -13.8) * mm});
            skLineSegment(sketch, "E137.right", {"start": v(43.8, -14.8) * mm, "end": v(43.8, -13.8) * mm});
            skSolve(sketch);
        }
        {
            var Q0;
            {var subQ13=sQuery(id+"F10.wireOp",EDGE,"E101.left");Q0=makeQuery(id+"F10.imprint","IMPRINT",FACE,{"disambiguationData":[TD([[makeQuery(id+"F10.imprint","IMPRINT",EDGE,{"derivedFrom":subQ13}),1.0]])]});}
            extrude(context, id + "F11", {"entities" : qUnion([Q0]), "operationType" : NewBodyOperationType.REMOVE, "oppositeDirection" : true, "depth" : 6 * mm, "offsetDistance" : 25.4 * mm});
        }
        {
            var Q0;
            {var subQ0=sQuery(id+"F8.wireOp",EDGE,"E97.right");var subQ1=sQuery(id+"F8.wireOp",EDGE,"E95.left");var subQ2=sQuery(id+"F6.wireOp",EDGE,"E63.top");var subQ3=sQuery(id+"F0.wireOp",EDGE,"E0.bottom");Q0=makeQuery(id+"F11.boolean.opBoolean","MERGE",FACE,{"derivedFrom":[makeQuery(id+"F7.boolean.opBoolean","COPY",FACE,{"derivedFrom":makeQuery(id+"F7.opExtrude","CAP_FACE",FACE,{"disambiguationData":[OSD([subQ3,sQuery(id+"F6.wireOp",EDGE,"E42.left"),sQuery(id+"F6.wireOp",EDGE,"E45.top"),sQuery(id+"F6.wireOp",EDGE,"E47.right"),sQuery(id+"F6.wireOp",EDGE,"E50"),sQuery(id+"F6.wireOp",EDGE,"E51.top"),sQuery(id+"F6.wireOp",EDGE,"E51.left"),sQuery(id+"F6.wireOp",EDGE,"E51.right"),sQuery(id+"F6.wireOp",EDGE,"E53.right"),sQuery(id+"F6.wireOp",EDGE,"E54"),sQuery(id+"F6.wireOp",EDGE,"E56.top"),sQuery(id+"F6.wireOp",EDGE,"E56.left"),sQuery(id+"F6.wireOp",EDGE,"E56.right"),sQuery(id+"F6.wireOp",EDGE,"E59.bottom"),sQuery(id+"F6.wireOp",EDGE,"E59.left"),sQuery(id+"F6.wireOp",EDGE,"E59.right"),sQuery(id+"F6.wireOp",EDGE,"E62.top"),sQuery(id+"F6.wireOp",EDGE,"E62.left"),sQuery(id+"F6.wireOp",EDGE,"E62.right"),subQ2,sQuery(id+"F6.wireOp",EDGE,"E66.top"),sQuery(id+"F6.wireOp",EDGE,"E66.left"),sQuery(id+"F6.wireOp",EDGE,"E66.right"),sQuery(id+"F6.wireOp",EDGE,"E69.top"),sQuery(id+"F6.wireOp",EDGE,"E69.left"),sQuery(id+"F6.wireOp",EDGE,"E69.right"),sQuery(id+"F6.wireOp",EDGE,"E72.top"),sQuery(id+"F6.wireOp",EDGE,"E72.left"),sQuery(id+"F6.wireOp",EDGE,"E72.right"),sQuery(id+"F6.wireOp",EDGE,"E75.left"),sQuery(id+"F6.wireOp",EDGE,"E77.top"),sQuery(id+"F6.wireOp",EDGE,"E77.left"),sQuery(id+"F6.wireOp",EDGE,"E77.right")])],"isStart":false})}),makeQuery(id+"F9.boolean.opBoolean","MERGE",FACE,{"derivedFrom":[makeQuery(id+"F7.boolean.opBoolean","COPY",FACE,{"derivedFrom":makeQuery(id+"F7.opExtrude","CAP_FACE",FACE,{"disambiguationData":[OSD([subQ3,sQuery(id+"F6.wireOp",EDGE,"E37.left"),sQuery(id+"F6.wireOp",EDGE,"E39.right"),sQuery(id+"F6.wireOp",EDGE,"E40")])],"isStart":false})}),makeQuery(id+"F9.opExtrude","CAP_FACE",FACE,{"disambiguationData":[OSD([sQuery(id+"F0.wireOp",EDGE,"E0.left"),sQuery(id+"F8.wireOp",EDGE,"E79.right"),sQuery(id+"F8.wireOp",EDGE,"E82.bottom"),sQuery(id+"F8.wireOp",EDGE,"E83"),sQuery(id+"F8.wireOp",EDGE,"E85.top"),sQuery(id+"F8.wireOp",EDGE,"E85.left"),sQuery(id+"F8.wireOp",EDGE,"E86"),sQuery(id+"F8.wireOp",EDGE,"E87.bottom"),sQuery(id+"F8.wireOp",EDGE,"E89.bottom"),sQuery(id+"F8.wireOp",EDGE,"E89.left"),sQuery(id+"F8.wireOp",EDGE,"E91"),sQuery(id+"F8.wireOp",EDGE,"E92"),sQuery(id+"F8.wireOp",EDGE,"E95.top"),subQ1,subQ0,sQuery(id+"F8.wireOp",EDGE,"E99"),sQuery(id+"F8.wireOp",EDGE,"E100")])],"isStart":false})]}),makeQuery(id+"F11.opExtrude","CAP_FACE",FACE,{"disambiguationData":[OSD([subQ2,subQ1,subQ0,sQuery(id+"F10.wireOp",EDGE,"E101.top"),sQuery(id+"F10.wireOp",EDGE,"E101.left"),sQuery(id+"F10.wireOp",EDGE,"E102.right"),sQuery(id+"F10.wireOp",EDGE,"E104.left"),sQuery(id+"F10.wireOp",EDGE,"E106.right"),sQuery(id+"F10.wireOp",EDGE,"E109.bottom"),sQuery(id+"F10.wireOp",EDGE,"E109.top"),sQuery(id+"F10.wireOp",EDGE,"E109.left"),sQuery(id+"F10.wireOp",EDGE,"E112.bottom"),sQuery(id+"F10.wireOp",EDGE,"E112.top"),sQuery(id+"F10.wireOp",EDGE,"E112.right"),sQuery(id+"F10.wireOp",EDGE,"E115.bottom"),sQuery(id+"F10.wireOp",EDGE,"E115.top"),sQuery(id+"F10.wireOp",EDGE,"E115.left"),sQuery(id+"F10.wireOp",EDGE,"E117.right"),sQuery(id+"F10.wireOp",EDGE,"E119.bottom"),sQuery(id+"F10.wireOp",EDGE,"E119.top"),sQuery(id+"F10.wireOp",EDGE,"E119.right"),sQuery(id+"F10.wireOp",EDGE,"E120.top"),sQuery(id+"F10.wireOp",EDGE,"E122.top"),sQuery(id+"F10.wireOp",EDGE,"E122.right"),sQuery(id+"F10.wireOp",EDGE,"E125.bottom"),sQuery(id+"F10.wireOp",EDGE,"E128.bottom"),sQuery(id+"F10.wireOp",EDGE,"E128.left"),sQuery(id+"F10.wireOp",EDGE,"E128.right"),sQuery(id+"F10.wireOp",EDGE,"E130.bottom"),sQuery(id+"F10.wireOp",EDGE,"E130.top"),sQuery(id+"F10.wireOp",EDGE,"E130.left"),sQuery(id+"F10.wireOp",EDGE,"E133.bottom"),sQuery(id+"F10.wireOp",EDGE,"E133.top"),sQuery(id+"F10.wireOp",EDGE,"E133.left"),sQuery(id+"F10.wireOp",EDGE,"E137.bottom"),sQuery(id+"F10.wireOp",EDGE,"E137.top"),sQuery(id+"F10.wireOp",EDGE,"E137.right")])],"isStart":false})]});}
            var sketch = newSketch(context, id + "F12", { "sketchPlane" : qUnion([Q0])});
            skLineSegment(sketch, "E138.bottom", {"start": v(26.8, -7.8) * mm, "end": v(4.2, -7.8) * mm});
            skLineSegment(sketch, "E138.top", {"start": v(26.8, -6.8) * mm, "end": v(4.2, -6.8) * mm});
            skLineSegment(sketch, "E138.left", {"start": v(26.8, -7.8) * mm, "end": v(26.8, -6.8) * mm});
            skLineSegment(sketch, "E138.right", {"start": v(4.2, -7.8) * mm, "end": v(4.2, -6.8) * mm});
            skSolve(sketch);
        }
        {
            var Q0;
            Q0 = qSketchRegion(id + "F12", true);
            extrude(context, id + "F13", {"entities" : qUnion([Q0]), "operationType" : NewBodyOperationType.ADD, "depth" : 6 * mm, "offsetDistance" : 25.4 * mm});
        }
        {
            var Q0;
            {var subQ12=sQuery(id+"F0.wireOp",EDGE,"E0.right");var subQ14=sQuery(id+"F0.wireOp",EDGE,"E0.left");var subQ20=sQuery(id+"F0.wireOp",EDGE,"E0.top");var subQ21=makeQuery(id+"F1.opExtrude","SWEPT_FACE",FACE,{"disambiguationData":[OSD([subQ20])]});var subQ26=sQuery(id+"F0.wireOp",EDGE,"E0.bottom");Q0=makeQuery(id+"F9.boolean.opBoolean","SPLIT",FACE,{"disambiguationData":[TD([subQ21])],"derivedFrom":makeQuery(id+"F5.boolean.opBoolean","SPLIT",FACE,{"disambiguationData":[TD([subQ21])],"derivedFrom":makeQuery(id+"F1.opExtrude","CAP_FACE",FACE,{"disambiguationData":[OSD([subQ26,subQ20,subQ14,subQ12])],"isStart":false})})});}
            var sketch = newSketch(context, id + "F14", { "sketchPlane" : qUnion([Q0])});
            skPoint(sketch, "E139", {"position": v(-29.8, -7.8) * mm});
            skLineSegment(sketch, "E140.bottom", {"start": v(-29.8, -7.8) * mm, "end": v(-50.8, -7.8) * mm});
            skLineSegment(sketch, "E140.top", {"start": v(-29.8, -6.8) * mm, "end": v(-50.8, -6.8) * mm});
            skLineSegment(sketch, "E140.left", {"start": v(-29.8, -7.8) * mm, "end": v(-29.8, -6.8) * mm});
            skLineSegment(sketch, "E140.right", {"start": v(-50.8, -7.8) * mm, "end": v(-50.8, -6.8) * mm});
            skLineSegment(sketch, "E141", {"start": v(-29.8, 14.2) * mm, "end": v(-29.8, -6.8) * mm});
            skPoint(sketch, "E142", {"position": v(-23.8, 14.2) * mm});
            skPoint(sketch, "E143", {"position": v(-22.8, -7.8) * mm});
            skLineSegment(sketch, "E144.bottom", {"start": v(-22.8, -7.8) * mm, "end": v(-23.8, -7.8) * mm});
            skLineSegment(sketch, "E144.top", {"start": v(-22.8, 14.2) * mm, "end": v(-23.8, 14.2) * mm});
            skLineSegment(sketch, "E144.left", {"start": v(-22.8, -7.8) * mm, "end": v(-22.8, 14.2) * mm});
            skLineSegment(sketch, "E144.right", {"start": v(-23.8, -7.8) * mm, "end": v(-23.8, 14.2) * mm});
            skPoint(sketch, "E145", {"position": v(20.8, -14.8) * mm});
            skLineSegment(sketch, "E146.bottom", {"start": v(20.8, -14.8) * mm, "end": v(19.8, -14.8) * mm});
            skLineSegment(sketch, "E146.top", {"start": v(20.8, -21.8) * mm, "end": v(19.8, -21.8) * mm});
            skLineSegment(sketch, "E146.left", {"start": v(20.8, -14.8) * mm, "end": v(20.8, -21.8) * mm});
            skLineSegment(sketch, "E146.right", {"start": v(19.8, -14.8) * mm, "end": v(19.8, -21.8) * mm});
            skPoint(sketch, "E147", {"position": v(-2.8, -13.8) * mm});
            skLineSegment(sketch, "E148.bottom", {"start": v(-2.8, -13.8) * mm, "end": v(20.8, -13.8) * mm});
            skLineSegment(sketch, "E148.top", {"start": v(-2.8, -14.8) * mm, "end": v(20.8, -14.8) * mm});
            skLineSegment(sketch, "E148.left", {"start": v(-2.8, -13.8) * mm, "end": v(-2.8, -14.8) * mm});
            skLineSegment(sketch, "E148.right", {"start": v(20.8, -13.8) * mm, "end": v(20.8, -14.8) * mm});
            skLineSegment(sketch, "E149.bottom", {"start": v(-2.8, -13.8) * mm, "end": v(-1.8, -13.8) * mm});
            skLineSegment(sketch, "E149.top", {"start": v(-2.8, 14.2) * mm, "end": v(-1.8, 14.2) * mm});
            skLineSegment(sketch, "E149.left", {"start": v(-2.8, -13.8) * mm, "end": v(-2.8, 14.2) * mm});
            skLineSegment(sketch, "E149.right", {"start": v(-1.8, -13.8) * mm, "end": v(-1.8, 14.2) * mm});
            skPoint(sketch, "E150", {"position": v(-22.8, 13.2) * mm});
            skLineSegment(sketch, "E151.bottom", {"start": v(-22.8, 13.2) * mm, "end": v(-2.8, 13.2) * mm});
            skLineSegment(sketch, "E151.top", {"start": v(-22.8, 14.2) * mm, "end": v(-2.8, 14.2) * mm});
            skLineSegment(sketch, "E151.left", {"start": v(-22.8, 13.2) * mm, "end": v(-22.8, 14.2) * mm});
            skLineSegment(sketch, "E151.right", {"start": v(-2.8, 13.2) * mm, "end": v(-2.8, 14.2) * mm});
            skPoint(sketch, "E152", {"position": v(-16.8, -13.8) * mm});
            skPoint(sketch, "E153", {"position": v(-43.8, -14.8) * mm});
            skLineSegment(sketch, "E154.bottom", {"start": v(-43.8, -14.8) * mm, "end": v(-16.8, -14.8) * mm});
            skLineSegment(sketch, "E154.top", {"start": v(-43.8, -13.8) * mm, "end": v(-16.8, -13.8) * mm});
            skLineSegment(sketch, "E154.left", {"start": v(-43.8, -14.8) * mm, "end": v(-43.8, -13.8) * mm});
            skLineSegment(sketch, "E154.right", {"start": v(-16.8, -14.8) * mm, "end": v(-16.8, -13.8) * mm});
            skPoint(sketch, "E155", {"position": v(-15.8, 7.2) * mm});
            skLineSegment(sketch, "E156.bottom", {"start": v(-15.8, 7.2) * mm, "end": v(-16.8, 7.2) * mm});
            skLineSegment(sketch, "E156.top", {"start": v(-15.8, -14.8) * mm, "end": v(-16.8, -14.8) * mm});
            skLineSegment(sketch, "E156.left", {"start": v(-15.8, 7.2) * mm, "end": v(-15.8, -14.8) * mm});
            skLineSegment(sketch, "E156.right", {"start": v(-16.8, 7.2) * mm, "end": v(-16.8, -14.8) * mm});
            skPoint(sketch, "E157", {"position": v(-8.8, 6.2) * mm});
            skLineSegment(sketch, "E158.bottom", {"start": v(-8.8, 6.2) * mm, "end": v(-15.8, 6.2) * mm});
            skLineSegment(sketch, "E158.top", {"start": v(-8.8, 7.2) * mm, "end": v(-15.8, 7.2) * mm});
            skLineSegment(sketch, "E158.left", {"start": v(-8.8, 6.2) * mm, "end": v(-8.8, 7.2) * mm});
            skLineSegment(sketch, "E158.right", {"start": v(-15.8, 6.2) * mm, "end": v(-15.8, 7.2) * mm});
            skPoint(sketch, "E159", {"position": v(-9.8, 0.2) * mm});
            skPoint(sketch, "E160", {"position": v(-2.8, -0.8) * mm});
            skLineSegment(sketch, "E161.bottom", {"start": v(-9.8, 0.2) * mm, "end": v(-2.8, 0.2) * mm});
            skLineSegment(sketch, "E161.top", {"start": v(-9.8, -0.8) * mm, "end": v(-2.8, -0.8) * mm});
            skLineSegment(sketch, "E161.left", {"start": v(-9.8, 0.2) * mm, "end": v(-9.8, -0.8) * mm});
            skLineSegment(sketch, "E161.right", {"start": v(-2.8, 0.2) * mm, "end": v(-2.8, -0.8) * mm});
            skPoint(sketch, "E162", {"position": v(-8.8, -6.8) * mm});
            skPoint(sketch, "E163", {"position": v(-15.8, -7.8) * mm});
            skLineSegment(sketch, "E164.bottom", {"start": v(-8.8, -6.8) * mm, "end": v(-15.8, -6.8) * mm});
            skLineSegment(sketch, "E164.top", {"start": v(-8.8, -7.8) * mm, "end": v(-15.8, -7.8) * mm});
            skLineSegment(sketch, "E164.left", {"start": v(-8.8, -6.8) * mm, "end": v(-8.8, -7.8) * mm});
            skLineSegment(sketch, "E164.right", {"start": v(-15.8, -6.8) * mm, "end": v(-15.8, -7.8) * mm});
            skPoint(sketch, "E165", {"position": v(-9.8, -14.8) * mm});
            skLineSegment(sketch, "E166.bottom", {"start": v(-9.8, -14.8) * mm, "end": v(-2.8, -14.8) * mm});
            skLineSegment(sketch, "E166.top", {"start": v(-9.8, -13.8) * mm, "end": v(-2.8, -13.8) * mm});
            skLineSegment(sketch, "E166.left", {"start": v(-9.8, -14.8) * mm, "end": v(-9.8, -13.8) * mm});
            skLineSegment(sketch, "E166.right", {"start": v(-2.8, -14.8) * mm, "end": v(-2.8, -13.8) * mm});
            skPoint(sketch, "E167", {"position": v(-16.8, -20.8) * mm});
            skLineSegment(sketch, "E168.bottom", {"start": v(-16.8, -20.8) * mm, "end": v(19.8, -20.8) * mm});
            skLineSegment(sketch, "E168.top", {"start": v(-16.8, -21.8) * mm, "end": v(19.8, -21.8) * mm});
            skLineSegment(sketch, "E168.left", {"start": v(-16.8, -20.8) * mm, "end": v(-16.8, -21.8) * mm});
            skLineSegment(sketch, "E168.right", {"start": v(19.8, -20.8) * mm, "end": v(19.8, -21.8) * mm});
            skLineSegment(sketch, "E169.top", {"start": v(-15.8, -20.8) * mm, "end": v(-16.8, -20.8) * mm});
            skLineSegment(sketch, "E169.left", {"start": v(-15.8, -14.8) * mm, "end": v(-15.8, -20.8) * mm});
            skLineSegment(sketch, "E169.right", {"start": v(-16.8, -14.8) * mm, "end": v(-16.8, -20.8) * mm});
            skPoint(sketch, "E170", {"position": v(-49.8, -20.8) * mm});
            skLineSegment(sketch, "E171.bottom", {"start": v(-49.8, -20.8) * mm, "end": v(-50.8, -20.8) * mm});
            skLineSegment(sketch, "E171.top", {"start": v(-49.8, -7.8) * mm, "end": v(-50.8, -7.8) * mm});
            skLineSegment(sketch, "E171.left", {"start": v(-49.8, -20.8) * mm, "end": v(-49.8, -7.8) * mm});
            skLineSegment(sketch, "E171.right", {"start": v(-50.8, -20.8) * mm, "end": v(-50.8, -7.8) * mm});
            skLineSegment(sketch, "E172.bottom", {"start": v(-50.8, -20.8) * mm, "end": v(-22.8, -20.8) * mm});
            skLineSegment(sketch, "E172.top", {"start": v(-50.8, -21.8) * mm, "end": v(-22.8, -21.8) * mm});
            skLineSegment(sketch, "E172.left", {"start": v(-50.8, -20.8) * mm, "end": v(-50.8, -21.8) * mm});
            skLineSegment(sketch, "E172.right", {"start": v(-22.8, -20.8) * mm, "end": v(-22.8, -21.8) * mm});
            skPoint(sketch, "E173", {"position": v(-8.2, -50.8) * mm});
            skLineSegment(sketch, "E174.bottom", {"start": v(-8.2, -50.8) * mm, "end": v(-7.2, -50.8) * mm});
            skLineSegment(sketch, "E174.top", {"start": v(-8.2, -21.8) * mm, "end": v(-7.2, -21.8) * mm});
            skLineSegment(sketch, "E174.left", {"start": v(-8.2, -50.8) * mm, "end": v(-8.2, -21.8) * mm});
            skLineSegment(sketch, "E174.right", {"start": v(-7.2, -50.8) * mm, "end": v(-7.2, -21.8) * mm});
            skPoint(sketch, "E175", {"position": v(-14.2, -27.8) * mm});
            skPoint(sketch, "E176", {"position": v(-15.2, -50.8) * mm});
            skLineSegment(sketch, "E177.bottom", {"start": v(-15.2, -50.8) * mm, "end": v(-14.2, -50.8) * mm});
            skLineSegment(sketch, "E177.top", {"start": v(-15.2, -27.8) * mm, "end": v(-14.2, -27.8) * mm});
            skLineSegment(sketch, "E177.left", {"start": v(-15.2, -50.8) * mm, "end": v(-15.2, -27.8) * mm});
            skLineSegment(sketch, "E177.right", {"start": v(-14.2, -50.8) * mm, "end": v(-14.2, -27.8) * mm});
            skPoint(sketch, "E178", {"position": v(-21.2, -27.8) * mm});
            skPoint(sketch, "E179", {"position": v(-22.2, -50.8) * mm});
            skLineSegment(sketch, "E180.bottom", {"start": v(-21.2, -27.8) * mm, "end": v(-22.2, -27.8) * mm});
            skLineSegment(sketch, "E180.top", {"start": v(-21.2, -50.8) * mm, "end": v(-22.2, -50.8) * mm});
            skLineSegment(sketch, "E180.left", {"start": v(-21.2, -27.8) * mm, "end": v(-21.2, -50.8) * mm});
            skLineSegment(sketch, "E180.right", {"start": v(-22.2, -27.8) * mm, "end": v(-22.2, -50.8) * mm});
            skPoint(sketch, "E181.positionSnap0", {"position": v(-30.3, -13.8) * mm});
            skPoint(sketch, "E182", {"position": v(-28.2, -27.8) * mm});
            skPoint(sketch, "E183", {"position": v(-29.2, -50.8) * mm});
            skLineSegment(sketch, "E184.bottom", {"start": v(-29.2, -50.8) * mm, "end": v(-28.2, -50.8) * mm});
            skLineSegment(sketch, "E184.top", {"start": v(-29.2, -27.8) * mm, "end": v(-28.2, -27.8) * mm});
            skLineSegment(sketch, "E184.left", {"start": v(-29.2, -50.8) * mm, "end": v(-29.2, -27.8) * mm});
            skLineSegment(sketch, "E184.right", {"start": v(-28.2, -50.8) * mm, "end": v(-28.2, -27.8) * mm});
            skPoint(sketch, "E185", {"position": v(-35.2, -27.8) * mm});
            skPoint(sketch, "E186", {"position": v(-36.2, -50.8) * mm});
            skLineSegment(sketch, "E187.bottom", {"start": v(-36.2, -50.8) * mm, "end": v(-35.2, -50.8) * mm});
            skLineSegment(sketch, "E187.top", {"start": v(-36.2, -27.8) * mm, "end": v(-35.2, -27.8) * mm});
            skLineSegment(sketch, "E187.left", {"start": v(-36.2, -50.8) * mm, "end": v(-36.2, -27.8) * mm});
            skLineSegment(sketch, "E187.right", {"start": v(-35.2, -50.8) * mm, "end": v(-35.2, -27.8) * mm});
            skPoint(sketch, "E188", {"position": v(-42.2, -27.8) * mm});
            skPoint(sketch, "E189", {"position": v(-43.2, -50.8) * mm});
            skLineSegment(sketch, "E190.bottom", {"start": v(-43.2, -50.8) * mm, "end": v(-42.2, -50.8) * mm});
            skLineSegment(sketch, "E190.top", {"start": v(-43.2, -27.8) * mm, "end": v(-42.2, -27.8) * mm});
            skLineSegment(sketch, "E190.left", {"start": v(-43.2, -50.8) * mm, "end": v(-43.2, -27.8) * mm});
            skLineSegment(sketch, "E190.right", {"start": v(-42.2, -50.8) * mm, "end": v(-42.2, -27.8) * mm});
            skLineSegment(sketch, "E191", {"start": v(-43.2, -27.8) * mm, "end": v(-43.2, -21.8) * mm});
            skLineSegment(sketch, "E192.bottom", {"start": v(-42.2, -27.8) * mm, "end": v(-43.2, -27.8) * mm});
            skLineSegment(sketch, "E192.top", {"start": v(-42.2, -21.8) * mm, "end": v(-43.2, -21.8) * mm});
            skLineSegment(sketch, "E192.left", {"start": v(-42.2, -27.8) * mm, "end": v(-42.2, -21.8) * mm});
            skSolve(sketch);
        }
        {
            var Q0;
            Q0=makeQuery(id+"F14.imprint","IMPRINT",FACE,{"disambiguationData":[TD([[makeQuery(id+"F14.imprint","IMPRINT",EDGE,{"derivedFrom":sQuery(id+"F14.wireOp",EDGE,"E140.bottom")}),1.0]])]});
            var Q1;
            {var subQ4=sQuery(id+"F14.wireOp",EDGE,"E190.left");Q1=makeQuery(id+"F14.imprint","IMPRINT",FACE,{"disambiguationData":[TD([[makeQuery(id+"F14.imprint","IMPRINT",EDGE,{"derivedFrom":subQ4}),1.0]])]});}
            extrude(context, id + "F15", {"entities" : qUnion([Q0, Q1]), "operationType" : NewBodyOperationType.REMOVE, "oppositeDirection" : true, "depth" : 6 * mm, "offsetDistance" : 25.4 * mm});
        }
    });
